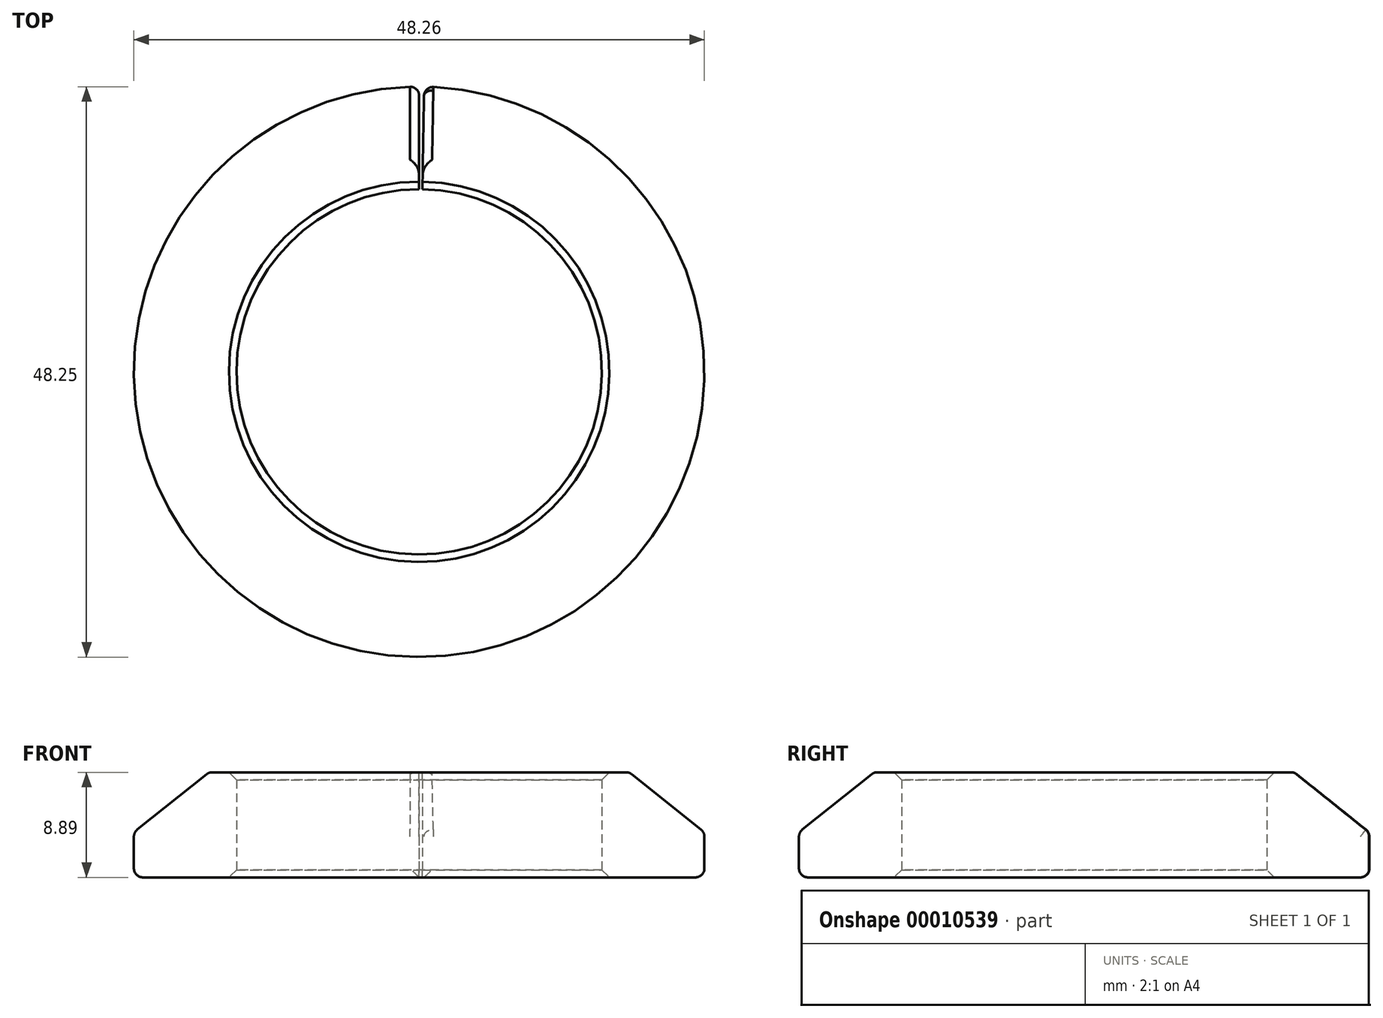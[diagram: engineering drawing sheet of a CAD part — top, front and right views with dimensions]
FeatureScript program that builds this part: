
annotation { "Feature Type Name" : "Feature", "Feature Type Description" : "" }
export const myFeature = defineFeature(function(context is Context, id is Id, definition is map)
    precondition{}
    {
        {
            var Q0;
            Q0=qCreatedBy(makeId("Right.planeOp"),FACE);
            var sketch = newSketch(context, id + "F0", { "sketchPlane" : qUnion([Q0])});
            skLineSegment(sketch, "E0", {"start": v(0, 0) * mm, "end": v(0, 42.85) * mm, "construction": true});
            skLineSegment(sketch, "E1", {"start": v(15.46, 0) * mm, "end": v(15.46, -8.9) * mm});
            skLineSegment(sketch, "E2", {"start": v(15.46, -8.9) * mm, "end": v(24.13, -8.9) * mm});
            skLineSegment(sketch, "E3", {"start": v(24.13, -8.9) * mm, "end": v(24.13, -5.08) * mm});
            skLineSegment(sketch, "E4", {"start": v(15.46, 0) * mm, "end": v(17.78, 0) * mm});
            skLineSegment(sketch, "E5", {"start": v(17.78, 0) * mm, "end": v(24.13, -5.08) * mm});
            skSolve(sketch);
        }
        {
            var Q0;
            Q0 = qSketchRegion(id + "F0", true);
            var Q1;
            Q1=sQuery(id+"F0.wireOp",EDGE,"E0");
            revolve(context, id + "F1", {"entities" : qUnion([Q0]), "axis" : qUnion([Q1]), "revolveType" : RevolveType.ONE_DIRECTION, "angle" : 359 * degree});
        }
        {
            var Q0;
            Q0=makeQuery(id+"F1.opRevolve","SWEPT_EDGE",EDGE,{"disambiguationData":[OSD([sQuery(id+"F0.wireOp",EDGE,"E1"),sQuery(id+"F0.wireOp",EDGE,"E4")])]});
            var Q1;
            Q1=makeQuery(id+"F1.opRevolve","SWEPT_EDGE",EDGE,{"disambiguationData":[OSD([sQuery(id+"F0.wireOp",EDGE,"E1"),sQuery(id+"F0.wireOp",EDGE,"E2")])]});
            chamfer(context, id + "F2", {"entities" : qUnion([Q0, Q1]), "width" : 0.64 * mm, "tangentPropagation" : true});
        }
        {
            var Q0;
            Q0=makeQuery(id+"F1.opRevolve","SWEPT_FACE",FACE,{"disambiguationData":[OSD([sQuery(id+"F0.wireOp",EDGE,"E3")])]});
            var Q1;
            Q1=makeQuery(id+"F1.opRevolve","SWEPT_FACE",FACE,{"disambiguationData":[OSD([sQuery(id+"F0.wireOp",EDGE,"E5")])]});
            fillet(context, id + "F3", {"entities" : qUnion([Q0, Q1]), "radius" : 0.76 * mm, "tangentPropagation" : true, "allowEdgeOverflow" : false});
        }
    });
